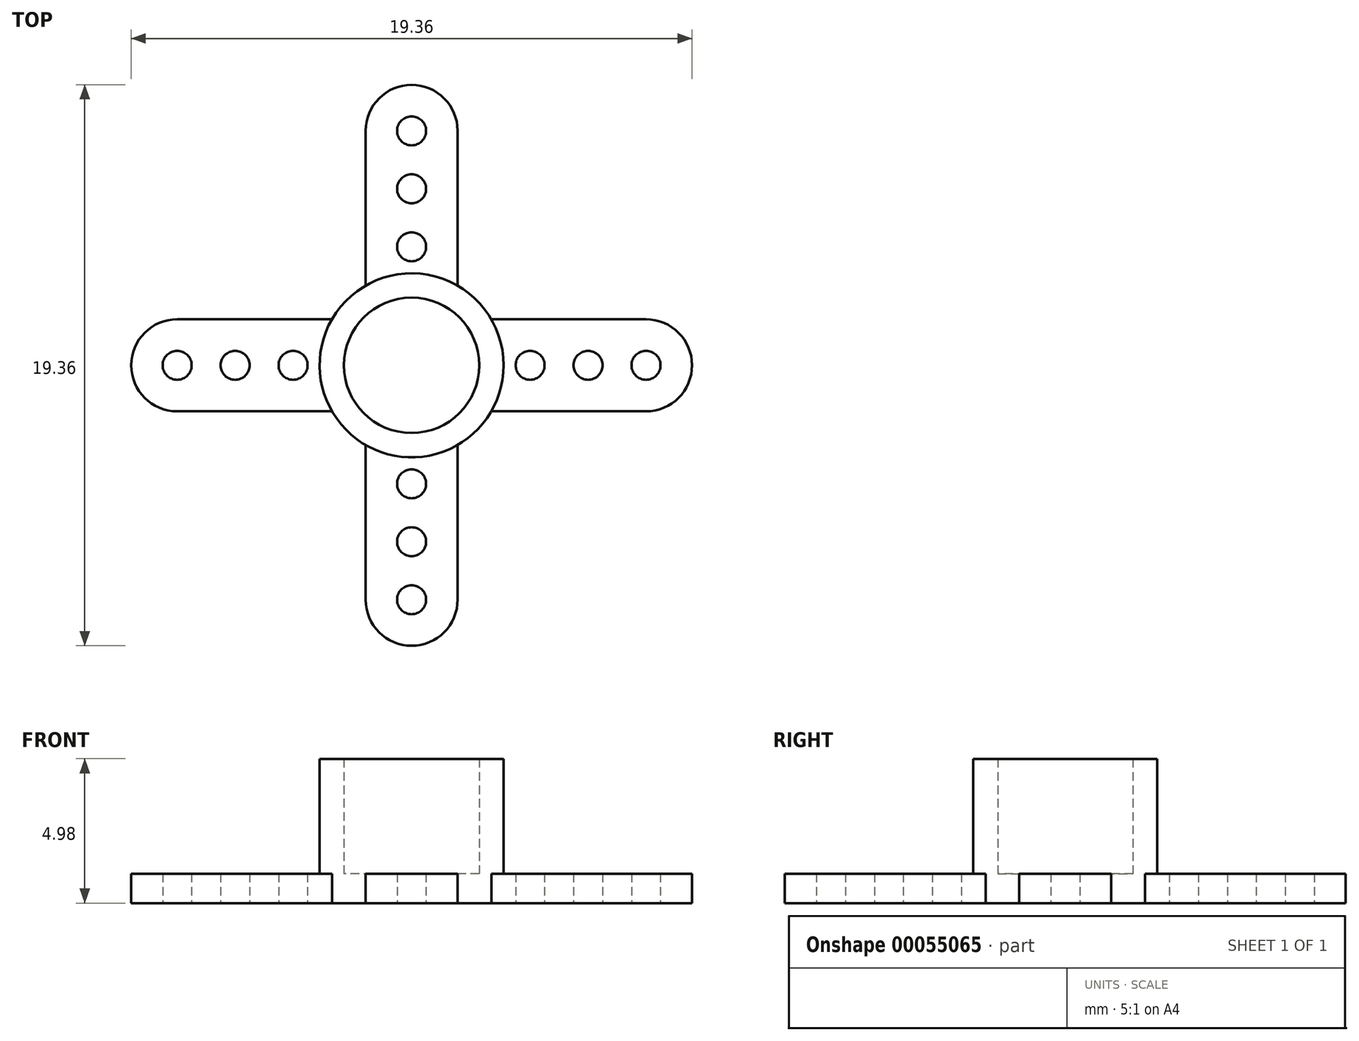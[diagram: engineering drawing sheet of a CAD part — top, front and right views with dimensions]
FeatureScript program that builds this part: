
annotation { "Feature Type Name" : "Feature", "Feature Type Description" : "" }
export const myFeature = defineFeature(function(context is Context, id is Id, definition is map)
    precondition{}
    {
        {
            var Q0;
            Q0=qCreatedBy(makeId("Top.planeOp"),FACE);
            var sketch = newSketch(context, id + "F0", { "sketchPlane" : qUnion([Q0])});
            skArc(sketch, "E0", {"start": v(1.59, 8.09) * mm, "mid": v(0, 9.68) * mm, "end": v(-1.59, 8.09) * mm});
            skArc(sketch, "E1", {"start": v(8.09, -1.59) * mm, "mid": v(9.68, 0) * mm, "end": v(8.09, 1.59) * mm});
            skArc(sketch, "E2", {"start": v(-1.59, -8.09) * mm, "mid": v(0, -9.68) * mm, "end": v(1.59, -8.09) * mm});
            skArc(sketch, "E3", {"start": v(-8.09, 1.59) * mm, "mid": v(-9.68, 0) * mm, "end": v(-8.09, -1.59) * mm});
            skArc(sketch, "E4", {"start": v(-2.75, -1.59) * mm, "mid": v(-2.25, -2.25) * mm, "end": v(-1.59, -2.75) * mm});
            skLineSegment(sketch, "E5", {"start": v(-8.09, 1.59) * mm, "end": v(-2.75, 1.59) * mm});
            skLineSegment(sketch, "E6", {"start": v(-8.09, -1.59) * mm, "end": v(-2.75, -1.59) * mm});
            skLineSegment(sketch, "E7", {"start": v(-1.59, -8.09) * mm, "end": v(-1.59, -2.75) * mm});
            skLineSegment(sketch, "E8", {"start": v(1.59, -8.09) * mm, "end": v(1.59, -2.75) * mm});
            skLineSegment(sketch, "E9", {"start": v(8.09, -1.59) * mm, "end": v(2.75, -1.59) * mm});
            skLineSegment(sketch, "E10", {"start": v(8.09, 1.59) * mm, "end": v(2.75, 1.59) * mm});
            skLineSegment(sketch, "E11", {"start": v(1.59, 8.09) * mm, "end": v(1.59, 2.75) * mm});
            skLineSegment(sketch, "E12", {"start": v(-1.59, 8.09) * mm, "end": v(-1.59, 2.75) * mm});
            skLineSegment(sketch, "E13", {"start": v(8.09, -1.59) * mm, "end": v(8.09, 1.59) * mm, "construction": true});
            skLineSegment(sketch, "E14", {"start": v(1.59, 8.09) * mm, "end": v(-1.59, 8.09) * mm, "construction": true});
            skLineSegment(sketch, "E15", {"start": v(-8.09, 1.59) * mm, "end": v(-8.09, -1.59) * mm, "construction": true});
            skLineSegment(sketch, "E16", {"start": v(-1.59, -8.09) * mm, "end": v(1.59, -8.09) * mm, "construction": true});
            skArc(sketch, "E17.trimOffspring", {"start": v(1.59, -2.75) * mm, "mid": v(2.25, -2.25) * mm, "end": v(2.75, -1.59) * mm});
            skArc(sketch, "E18.trimOffspring", {"start": v(-1.59, 2.75) * mm, "mid": v(-2.25, 2.25) * mm, "end": v(-2.75, 1.59) * mm});
            skArc(sketch, "E19.trimOffspring", {"start": v(2.75, 1.59) * mm, "mid": v(2.25, 2.25) * mm, "end": v(1.59, 2.75) * mm});
            skCircle(sketch, "E20", {"center": v(-8.09, 0) * mm, "radius": 0.5 * mm});
            skCircle(sketch, "E21", {"center": v(-6.09, 0) * mm, "radius": 0.5 * mm});
            skCircle(sketch, "E22", {"center": v(-4.09, 0) * mm, "radius": 0.5 * mm});
            skLineSegment(sketch, "E23", {"start": v(-8.09, 0) * mm, "end": v(-6.09, 0) * mm, "construction": true});
            skLineSegment(sketch, "E24", {"start": v(-4.09, 0) * mm, "end": v(-6.09, 0) * mm, "construction": true});
            skCircle(sketch, "E25.1.0", {"center": v(0, -4.09) * mm, "radius": 0.5 * mm});
            skCircle(sketch, "E25.1.1", {"center": v(0, -6.09) * mm, "radius": 0.5 * mm});
            skCircle(sketch, "E25.1.2", {"center": v(0, -8.09) * mm, "radius": 0.5 * mm});
            skCircle(sketch, "E25.2.0", {"center": v(4.09, 0) * mm, "radius": 0.5 * mm});
            skCircle(sketch, "E25.2.1", {"center": v(6.09, 0) * mm, "radius": 0.5 * mm});
            skCircle(sketch, "E25.2.2", {"center": v(8.09, 0) * mm, "radius": 0.5 * mm});
            skCircle(sketch, "E26.1.3.0", {"center": v(0, 4.09) * mm, "radius": 0.5 * mm});
            skCircle(sketch, "E26.2.3.0", {"center": v(0, 6.09) * mm, "radius": 0.5 * mm});
            skCircle(sketch, "E26.4.3.0", {"center": v(0, 8.09) * mm, "radius": 0.5 * mm});
            skSolve(sketch);
        }
        {
            var Q0;
            Q0 = qSketchRegion(id + "F0", true);
            extrude(context, id + "F1", {"entities" : qUnion([Q0]), "depth" : 1.02 * mm});
        }
        {
            var Q0;
            Q0=makeQuery(id+"F1.opExtrude","CAP_FACE",FACE,{"disambiguationData":[OSD([sQuery(id+"F0.wireOp",EDGE,"E0"),sQuery(id+"F0.wireOp",EDGE,"E1"),sQuery(id+"F0.wireOp",EDGE,"E2"),sQuery(id+"F0.wireOp",EDGE,"E3"),sQuery(id+"F0.wireOp",EDGE,"E4"),sQuery(id+"F0.wireOp",EDGE,"E5"),sQuery(id+"F0.wireOp",EDGE,"E6"),sQuery(id+"F0.wireOp",EDGE,"E7"),sQuery(id+"F0.wireOp",EDGE,"E8"),sQuery(id+"F0.wireOp",EDGE,"E9"),sQuery(id+"F0.wireOp",EDGE,"E10"),sQuery(id+"F0.wireOp",EDGE,"E11"),sQuery(id+"F0.wireOp",EDGE,"E12"),sQuery(id+"F0.wireOp",EDGE,"E17.trimOffspring"),sQuery(id+"F0.wireOp",EDGE,"E18.trimOffspring"),sQuery(id+"F0.wireOp",EDGE,"E19.trimOffspring"),sQuery(id+"F0.wireOp",EDGE,"E20"),sQuery(id+"F0.wireOp",EDGE,"E21"),sQuery(id+"F0.wireOp",EDGE,"E22"),sQuery(id+"F0.wireOp",EDGE,"E25.1.0"),sQuery(id+"F0.wireOp",EDGE,"E25.1.1"),sQuery(id+"F0.wireOp",EDGE,"E25.1.2"),sQuery(id+"F0.wireOp",EDGE,"E25.2.0"),sQuery(id+"F0.wireOp",EDGE,"E25.2.1"),sQuery(id+"F0.wireOp",EDGE,"E25.2.2"),sQuery(id+"F0.wireOp",EDGE,"E26.1.3.0"),sQuery(id+"F0.wireOp",EDGE,"E26.2.3.0"),sQuery(id+"F0.wireOp",EDGE,"E26.4.3.0")])],"isStart":false});
            var sketch = newSketch(context, id + "F2", { "sketchPlane" : qUnion([Q0])});
            skCircle(sketch, "E27", {"center": v(0, 0) * mm, "radius": 3.18 * mm});
            skCircle(sketch, "E28", {"center": v(0, 0) * mm, "radius": 2.33 * mm});
            skSolve(sketch);
        }
        {
            var Q0;
            Q0=makeQuery(id+"F2.imprint","IMPRINT",FACE,{"disambiguationData":[TD([[makeQuery(id+"F2.imprint","IMPRINT",EDGE,{"derivedFrom":sQuery(id+"F2.wireOp",EDGE,"E28")}),-1.0]])]});
            extrude(context, id + "F3", {"entities" : qUnion([Q0]), "operationType" : NewBodyOperationType.ADD, "depth" : 3.96 * mm});
        }
    });
